# Revit family: Gira_267703
name_source: partatom
category: Elektroinstallationen
revit_build: Autodesk Revit 2017 (Build: 20160225_1515(x64)
units: mm (PartAtom-declared; Revit-internal decimal feet)

## family parameters
Basisbauteil = Fläche
Beim Laden mit Abzugskörper schneiden = Nein
Bemaßung runder Anschluss = Durchmesser verwenden
Beschriftungsausrichtung beibehalten = Ja
Gemeinsam genutzt = Nein
Raumberechnungspunkt = Nein
Teiletyp = Normal

## types (1)
- Gira_267703
    Antibacterial treatment = Nein
    BIM = https://media.stage.bim.site
    Beschreibung = RCD-prot.sock.30mA SH Sys55 PW,RCD-protected socket outlet 30 mA with integrated increased contact protection (shutter) and symbol ,,pure white glossy,Features:,- The RCD-protected socket outlet is a permanently installed protective device with voltage-dependent residual current tripping in accordance with VDE0664.,- This device works like an RCD switch.,- Additional SCHUKO socket outlets can be connected to the connection wires, which are then also included in the residual current protection.,,Notes :,- Installation in a deep device box.,- Increased contact protection pursuant to DIN-VDE 0620-1.
    Colour = White
    Connection type = Plug clamp
    Cremeweiß glänzend = Cremeweiß glänzend
    Data sheet = https://katalog.gira.de
    Eject-mechanism = Nein
    Fault current protection = Ja
    Frequency [Hz] = [50:60]
    Für "erschwerte Bedingungen" (nach VDE) (*de-DE) = Nein
    GTIN = 4010337011958
    HAN = 267703
    Halogen free = Ja
    Hersteller = Gira
    Imprint/indication = Without imprint
    Insulated mounting = Nein
    Label space/information surface = Nein
    Lockable = Nein
    Material = Plastic
    Material quality = Thermoplastic
    Model = Other
    Mounting method = Flush mounted (plaster)
    Nominal current = 16 A
    Nominal voltage [Volt] = 230
    Number of modules (module system) = 1
    Number of socket outlets switchable = 0
    Number of units = 1
    Over voltage protection = Nein
    Productwebsite = http://katalog.gira.de
    Protective earth pin round = Nein
    RAL-number (akin) = 9010
    Rated fault current = 0 A
    Rotated central insert = Nein
    Special power supply = No special power supply
    Suitable for degree of protection (IP) = IP20
    Surface finishing = Glossy
    Surface protection = Other
    Transparent = Nein
    Type of fastening = Mounting with claw and screw
    Typname = RCD-prot.sock. 30 mA SH System 55 p.white
    URL = https://www.gira.de
    Vorgabe-Ansicht = 1219 mm
    With built-in USB power supply = Nein
    With child-protection = Ja
    With function lighting = Nein
    With hinged lid = Nein
    With loop through function = Nein
    With miniature fuse = Nein
    With on/off switch = Nein
    With orientation lighting = Nein
    With signal lamp = Ja

## geometry (parser evidence)
native form markers: Sweep x3
no freeform markers — native parametric forms only
